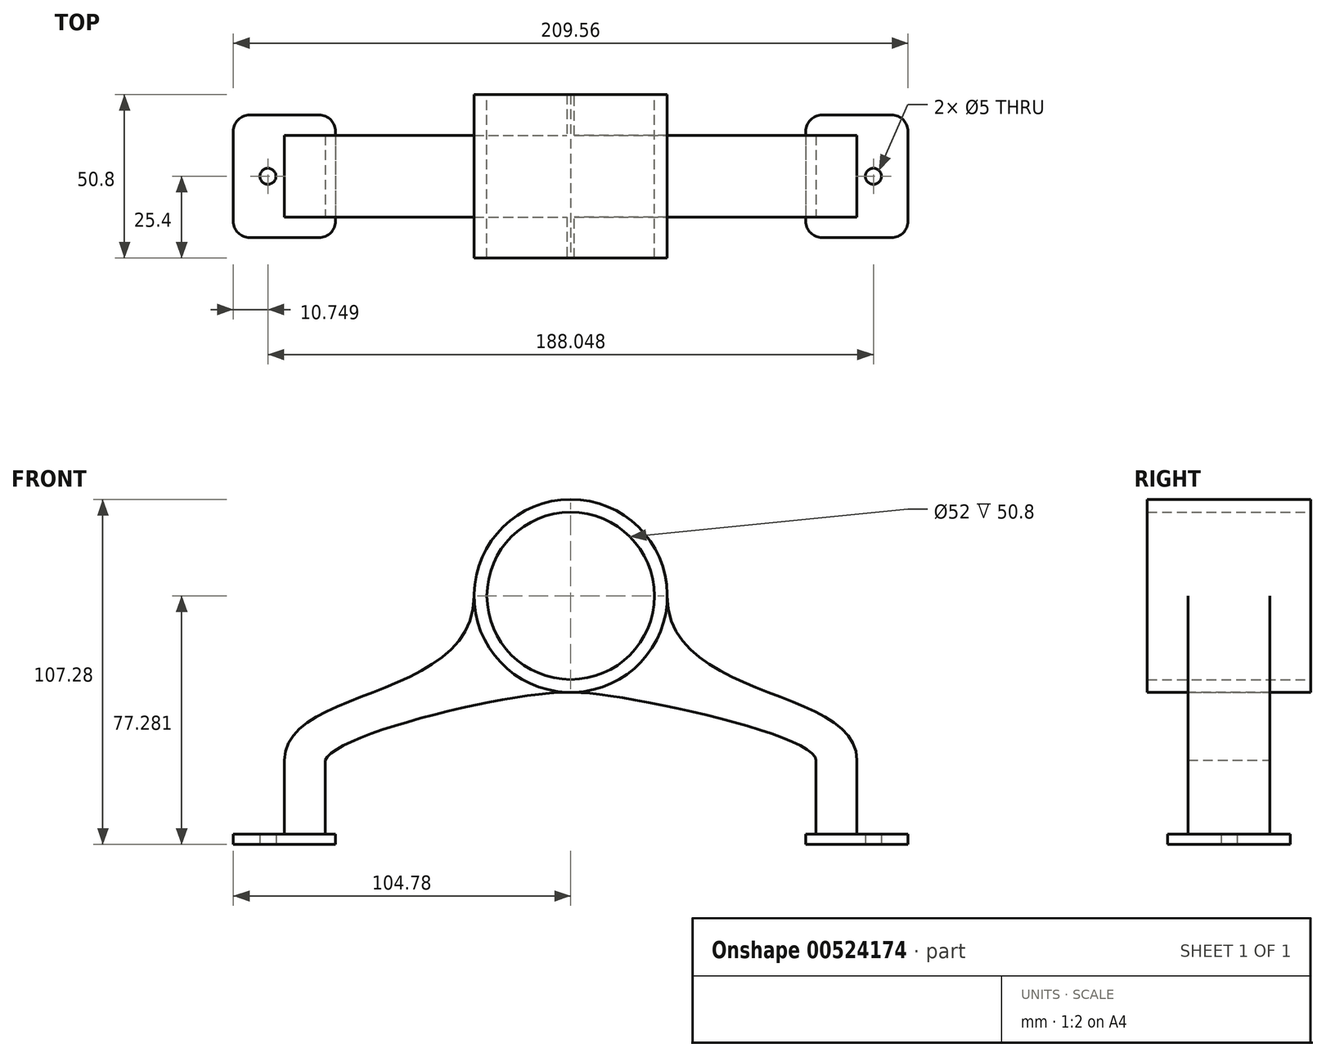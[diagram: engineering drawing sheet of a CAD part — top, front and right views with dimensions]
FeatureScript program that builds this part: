
annotation { "Feature Type Name" : "Feature", "Feature Type Description" : "" }
export const myFeature = defineFeature(function(context is Context, id is Id, definition is map)
    precondition{}
    {
        {
            var Q0;
            Q0=qCreatedBy(makeId("Front.planeOp"),FACE);
            var sketch = newSketch(context, id + "F0", { "sketchPlane" : qUnion([Q0])});
            skCircle(sketch, "E0", {"center": v(0, 51.11) * mm, "radius": 26 * mm});
            skCircle(sketch, "E1", {"center": v(0, 51.11) * mm, "radius": 30 * mm});
            skFitSpline(sketch, "E2", {"points": [v(-30, 51.11) * mm, v(-88.9, 0) * mm], "startDerivative": vector(0, -97.77) * mm, "endDerivative": vector(0, -68.8) * mm});
            skFitSpline(sketch, "E3", {"points": [v(30, 51.11) * mm, v(88.9, 0) * mm], "startDerivative": vector(0, -97.77) * mm, "endDerivative": vector(0, -68.8) * mm});
            skLineSegment(sketch, "E4", {"start": v(-88.9, 0) * mm, "end": v(-88.9, -26.17) * mm});
            skLineSegment(sketch, "E5", {"start": v(-88.9, -26.17) * mm, "end": v(-76.2, -26.17) * mm});
            skLineSegment(sketch, "E6", {"start": v(-76.2, -26.17) * mm, "end": v(-76.2, 0) * mm});
            skLineSegment(sketch, "E7", {"start": v(88.9, 0) * mm, "end": v(88.9, -26.17) * mm});
            skLineSegment(sketch, "E8", {"start": v(88.9, -26.17) * mm, "end": v(76.2, -26.17) * mm});
            skLineSegment(sketch, "E9", {"start": v(76.2, -26.17) * mm, "end": v(76.2, 0) * mm});
            skFitSpline(sketch, "E10", {"points": [v(-76.2, 0) * mm, v(0, 21.11) * mm], "startDerivative": vector(8.17, 24.91) * mm, "endDerivative": vector(51.52, -1.87) * mm});
            skFitSpline(sketch, "E11", {"points": [v(76.2, 0) * mm, v(0, 21.11) * mm], "startDerivative": vector(0, 24.91) * mm, "endDerivative": vector(-37.71, -1.87) * mm});
            skSolve(sketch);
        }
        {
            var Q0;
            Q0=makeQuery(id+"F0.imprint","IMPRINT",FACE,{"disambiguationData":[TD([[makeQuery(id+"F0.imprint","IMPRINT",EDGE,{"derivedFrom":sQuery(id+"F0.wireOp",EDGE,"E0")}),-1.0]])]});
            extrude(context, id + "F1", {"entities" : qUnion([Q0]), "endBound" : BoundingType.SYMMETRIC, "depth" : 50.8 * mm});
        }
        {
            var Q0;
            {var subQ0=sQuery(id+"F0.wireOp",EDGE,"E2");Q0=makeQuery(id+"F0.imprint","IMPRINT",FACE,{"disambiguationData":[TD([[makeQuery(id+"F0.imprint","IMPRINT",EDGE,{"derivedFrom":subQ0}),1.0]])]});}
            var Q1;
            {var subQ0=sQuery(id+"F0.wireOp",EDGE,"E3");Q1=makeQuery(id+"F0.imprint","IMPRINT",FACE,{"disambiguationData":[TD([[makeQuery(id+"F0.imprint","IMPRINT",EDGE,{"derivedFrom":subQ0}),-1.0]])]});}
            extrude(context, id + "F2", {"entities" : qUnion([Q0, Q1]), "operationType" : NewBodyOperationType.ADD, "endBound" : BoundingType.SYMMETRIC, "depth" : 25.4 * mm});
        }
        {
            var Q0;
            Q0=makeQuery(id+"F2.opExtrude","SWEPT_FACE",FACE,{"disambiguationData":[OSD([sQuery(id+"F0.wireOp",EDGE,"E5")])]});
            var sketch = newSketch(context, id + "F3", { "sketchPlane" : qUnion([Q0])});
            skPoint(sketch, "E12.middle", {"position": v(-88.9, 0) * mm});
            skLineSegment(sketch, "E13", {"start": v(0, -42.78) * mm, "end": v(0, 35) * mm, "construction": true});
            skLineSegment(sketch, "E14.bottom", {"start": v(-73.03, -19.05) * mm, "end": v(-104.78, -19.05) * mm});
            skLineSegment(sketch, "E14.top", {"start": v(-73.03, 19.05) * mm, "end": v(-104.78, 19.05) * mm});
            skLineSegment(sketch, "E14.left", {"start": v(-73.03, -19.05) * mm, "end": v(-73.03, 19.05) * mm});
            skLineSegment(sketch, "E14.right", {"start": v(-104.78, -19.05) * mm, "end": v(-104.78, 19.05) * mm});
            skLineSegment(sketch, "E15.MirrorCS", {"start": v(73.03, -19.05) * mm, "end": v(104.78, -19.05) * mm});
            skLineSegment(sketch, "E16.MirrorCS", {"start": v(104.78, -19.05) * mm, "end": v(104.78, 19.05) * mm});
            skLineSegment(sketch, "E17.MirrorCS", {"start": v(73.03, -19.05) * mm, "end": v(73.03, 19.05) * mm});
            skLineSegment(sketch, "E18.MirrorCS", {"start": v(73.03, 19.05) * mm, "end": v(104.78, 19.05) * mm});
            skSolve(sketch);
        }
        {
            var Q0;
            Q0=qSketchRegion(id+"F3",true);
            extrude(context, id + "F4", {"entities" : qUnion([Q0]), "operationType" : NewBodyOperationType.ADD, "oppositeDirection" : true, "depth" : 3.17 * mm});
        }
        {
            var Q0;
            Q0=makeQuery(id+"F4.opExtrude","SWEPT_EDGE",EDGE,{"disambiguationData":[OSD([sQuery(id+"F3.wireOp",EDGE,"E14.top"),sQuery(id+"F3.wireOp",EDGE,"E14.right")])]});
            var Q1;
            Q1=makeQuery(id+"F4.opExtrude","SWEPT_EDGE",EDGE,{"disambiguationData":[OSD([sQuery(id+"F3.wireOp",EDGE,"E14.top"),sQuery(id+"F3.wireOp",EDGE,"E14.left")])]});
            var Q2;
            Q2=makeQuery(id+"F4.opExtrude","SWEPT_EDGE",EDGE,{"disambiguationData":[OSD([sQuery(id+"F3.wireOp",EDGE,"E14.bottom"),sQuery(id+"F3.wireOp",EDGE,"E14.right")])]});
            var Q3;
            Q3=makeQuery(id+"F4.opExtrude","SWEPT_EDGE",EDGE,{"disambiguationData":[OSD([sQuery(id+"F3.wireOp",EDGE,"E14.bottom"),sQuery(id+"F3.wireOp",EDGE,"E14.left")])]});
            fillet(context, id + "F5", {"entities" : qUnion([Q0, Q1, Q2, Q3]), "radius" : 5.08 * mm, "tangentPropagation" : true, "allowEdgeOverflow" : false});
        }
        {
            var Q0;
            Q0=makeQuery(id+"F4.opExtrude","SWEPT_EDGE",EDGE,{"disambiguationData":[OSD([sQuery(id+"F3.wireOp",EDGE,"E16.MirrorCS"),sQuery(id+"F3.wireOp",EDGE,"E18.MirrorCS")])]});
            var Q1;
            Q1=makeQuery(id+"F4.opExtrude","SWEPT_EDGE",EDGE,{"disambiguationData":[OSD([sQuery(id+"F3.wireOp",EDGE,"E17.MirrorCS"),sQuery(id+"F3.wireOp",EDGE,"E18.MirrorCS")])]});
            var Q2;
            Q2=makeQuery(id+"F4.opExtrude","SWEPT_EDGE",EDGE,{"disambiguationData":[OSD([sQuery(id+"F3.wireOp",EDGE,"E15.MirrorCS"),sQuery(id+"F3.wireOp",EDGE,"E16.MirrorCS")])]});
            var Q3;
            Q3=makeQuery(id+"F4.opExtrude","SWEPT_EDGE",EDGE,{"disambiguationData":[OSD([sQuery(id+"F3.wireOp",EDGE,"E15.MirrorCS"),sQuery(id+"F3.wireOp",EDGE,"E17.MirrorCS")])]});
            fillet(context, id + "F6", {"entities" : qUnion([Q0, Q1, Q2, Q3]), "radius" : 5.08 * mm, "tangentPropagation" : true, "allowEdgeOverflow" : false});
        }
        {
            var Q0;
            Q0=makeQuery(id+"F4.boolean.opBoolean","MERGE",FACE,{"derivedFrom":[makeQuery(id+"F2.opExtrude","SWEPT_FACE",FACE,{"disambiguationData":[OSD([sQuery(id+"F0.wireOp",EDGE,"E5")])]}),makeQuery(id+"F4.opExtrude","CAP_FACE",FACE,{"disambiguationData":[OSD([sQuery(id+"F3.wireOp",EDGE,"E14.bottom"),sQuery(id+"F3.wireOp",EDGE,"E14.top"),sQuery(id+"F3.wireOp",EDGE,"E14.left"),sQuery(id+"F3.wireOp",EDGE,"E14.right")])],"isStart":true})]});
            var sketch = newSketch(context, id + "F7", { "sketchPlane" : qUnion([Q0])});
            skCircle(sketch, "E19", {"center": v(-94.03, 0) * mm, "radius": 2.5 * mm});
            skPoint(sketch, "E19.centerSnap0", {"position": v(-104.78, 0) * mm});
            skCircle(sketch, "E20", {"center": v(94.02, 0) * mm, "radius": 2.5 * mm});
            skSolve(sketch);
        }
        {
            var Q0;
            Q0=qSketchRegion(id+"F7",true);
            extrude(context, id + "F8", {"entities" : qUnion([Q0]), "operationType" : NewBodyOperationType.REMOVE, "oppositeDirection" : true, "depth" : 25.4 * mm});
        }
    });
